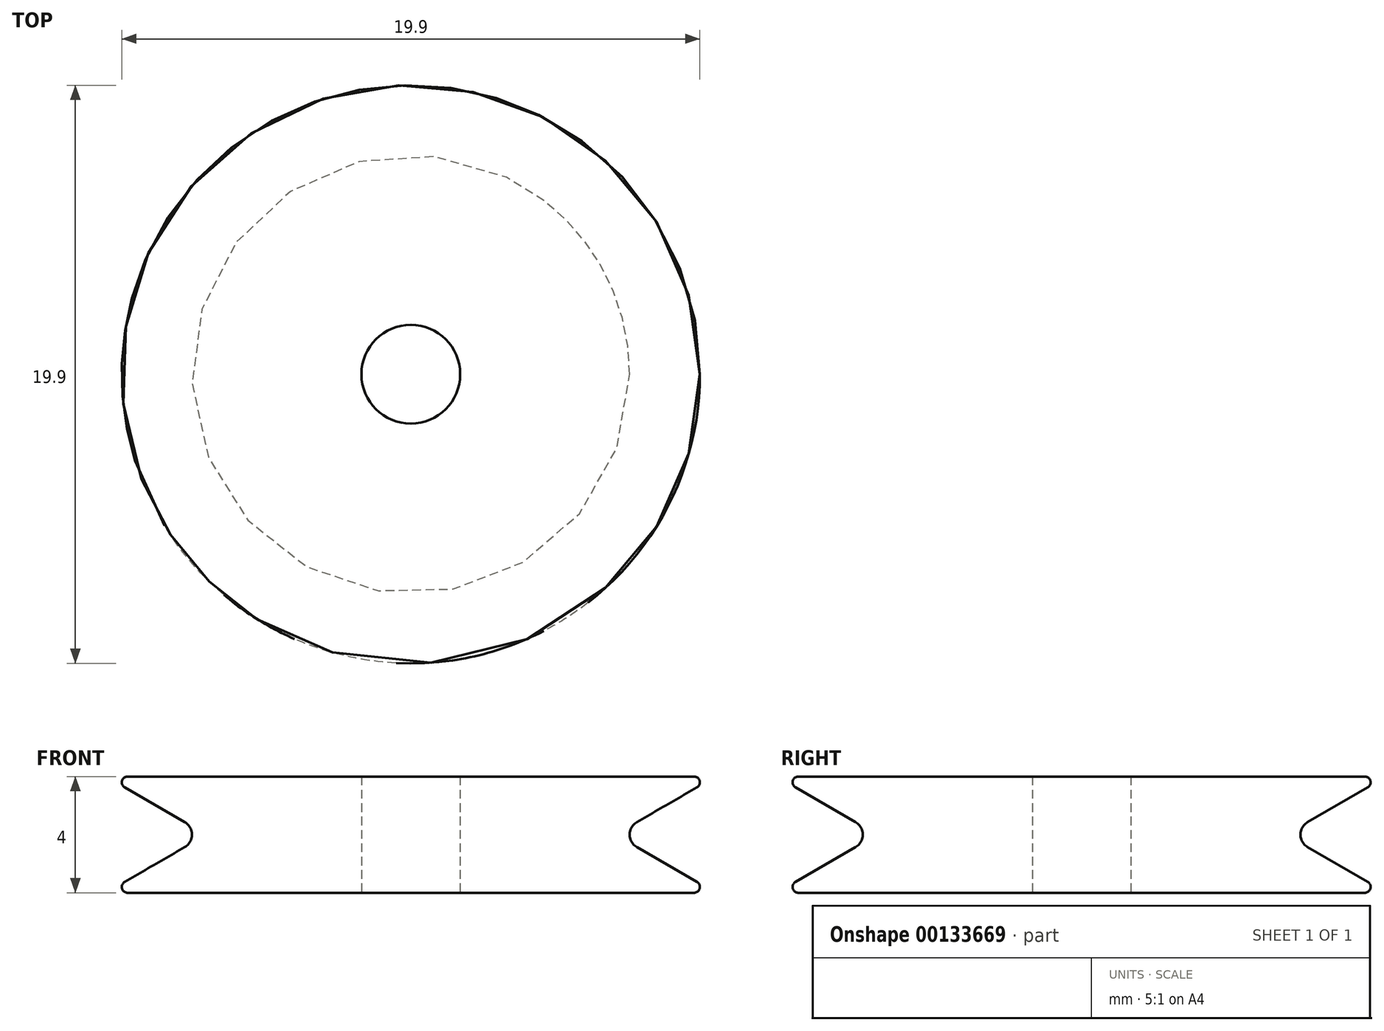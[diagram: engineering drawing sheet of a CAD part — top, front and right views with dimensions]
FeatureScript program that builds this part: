
annotation { "Feature Type Name" : "Feature", "Feature Type Description" : "" }
export const myFeature = defineFeature(function(context is Context, id is Id, definition is map)
    precondition{}
    {
        {
            var Q0;
            Q0=qCreatedBy(makeId("Top.planeOp"),FACE);
            var sketch = newSketch(context, id + "F0", { "sketchPlane" : qUnion([Q0])});
            skCircle(sketch, "E0", {"center": v(0, 0) * mm, "radius": 1.7 * mm});
            skCircle(sketch, "E1", {"center": v(0, 0) * mm, "radius": 10.5 * mm});
            skSolve(sketch);
        }
        {
            var Q0;
            Q0=makeQuery(id+"F0.imprint","IMPRINT",FACE,{"disambiguationData":[TD([[makeQuery(id+"F0.imprint","IMPRINT",EDGE,{"derivedFrom":sQuery(id+"F0.wireOp",EDGE,"E0")}),-1.0]])]});
            extrude(context, id + "F1", {"entities" : qUnion([Q0]), "depth" : 4 * mm});
        }
        {
            var Q0;
            Q0=qCreatedBy(makeId("Front.planeOp"),FACE);
            var sketch = newSketch(context, id + "F2", { "sketchPlane" : qUnion([Q0])});
            skLineSegment(sketch, "E2", {"start": v(-10.5, 0) * mm, "end": v(-7.04, 2) * mm});
            skLineSegment(sketch, "E3", {"start": v(-7.04, 2) * mm, "end": v(-10.5, 4) * mm});
            skLineSegment(sketch, "E4", {"start": v(-10.5, 0) * mm, "end": v(-10.5, 4) * mm});
            skLineSegment(sketch, "E5", {"start": v(-10.5, 0) * mm, "end": v(0, 0) * mm});
            skSolve(sketch);
        }
        {
            var Q0;
            Q0 = qSketchRegion(id + "F2", true);
            var Q1;
            Q1=makeQuery(id+"F1.opExtrude","CAP_EDGE",EDGE,{"disambiguationData":[OSD([sQuery(id+"F0.wireOp",EDGE,"E1")])],"isStart":false});
            revolve(context, id + "F3", {"operationType" : NewBodyOperationType.REMOVE, "entities" : qUnion([Q0]), "axis" : qUnion([Q1]), "revolveType" : RevolveType.FULL, "oppositeDirection" : true});
        }
        {
            var Q0;
            Q0=makeQuery(id+"F3.boolean.opBoolean","MERGE",EDGE,{"derivedFrom":[makeQuery(id+"F1.opExtrude","CAP_EDGE",EDGE,{"disambiguationData":[OSD([sQuery(id+"F0.wireOp",EDGE,"E1")])],"isStart":false}),makeQuery(id+"F3.opRevolve","SWEPT_EDGE",EDGE,{"disambiguationData":[OSD([sQuery(id+"F2.wireOp",EDGE,"E3"),sQuery(id+"F2.wireOp",EDGE,"E4")])]})]});
            var Q1;
            Q1=makeQuery(id+"F3.boolean.opBoolean","MERGE",EDGE,{"derivedFrom":[makeQuery(id+"F1.opExtrude","CAP_EDGE",EDGE,{"disambiguationData":[OSD([sQuery(id+"F0.wireOp",EDGE,"E1")])],"isStart":true}),makeQuery(id+"F3.opRevolve","SWEPT_EDGE",EDGE,{"disambiguationData":[OSD([sQuery(id+"F2.wireOp",EDGE,"E2"),sQuery(id+"F2.wireOp",EDGE,"E4")])]})]});
            fillet(context, id + "F4", {"entities" : qUnion([Q0, Q1]), "radius" : .2 * mm, "tangentPropagation" : true, "allowEdgeOverflow" : false});
        }
        {
            var Q0;
            Q0=makeQuery(id+"F3.boolean.opBoolean","COPY",EDGE,{"derivedFrom":makeQuery(id+"F3.opRevolve","SWEPT_EDGE",EDGE,{"disambiguationData":[OSD([sQuery(id+"F2.wireOp",EDGE,"E2"),sQuery(id+"F2.wireOp",EDGE,"E3")])]})});
            fillet(context, id + "F5", {"entities" : qUnion([Q0]), "radius" : .5 * mm, "tangentPropagation" : true, "allowEdgeOverflow" : false});
        }
    });
